# Revit family: IS_Dea_T0598_BIM_GB
name_source: partatom
category: Plumbing Fixtures
revit_build: Autodesk Revit MEP 2012 (Build: 20110309_2315(x64)
units: mm (PartAtom-declared; Revit-internal decimal feet)

## types (2) — shared parameters
Accessories = www.idealspec.co.uk
AreaUnits = millimeters
Assembly Code = C1030200
AssetType = Fixed
BIMObjectName = ISI_IdealStandard_Bidets_Dea-WallHung_T059801
BidetMounting = WallHung
Brand = Ideal Standard
CodePerformance = Vitreous china to BS 3402. Bidet to BS EN 36
Color = White
ConnectionType = Plumbing
Default Elevation = 400 mm  [stored 1.31234 ft]
Description = Dea wall-hung bidet with ceramic waste cover
DrainSize = 32 mm  [stored 0.104987 ft]
DurationUnit = year
ECA = No
ExpectedLife = 30
Features = Wall-hung bidet with ceramic waste cover
Finish = White
IfcExportAs = IfcSanitaryTerminalType
IfcExportType = BIDET
InstallationInstructions = www.idealspec.co.uk/resources.html
LinearUnits = millimeters
ManufacturerURL = www.idealspec.co.uk
Material = Vitreous china
ModelReference = Dea wall-hung bidet with ceramic waste cover
NBSDescription = Bidets
NBSReference = 45-35-70/320
Name = Bidets_Dea-WallHung_IdealStandard
NettWeight = 17.2 Kg
NominalHeight = 310 mm
NominalLength = 540 mm  [stored 1.77165 ft]
NominalWidth = 360 mm
Shape = Sculptured
Size = 310 x 540 x 360 cm
Space = Internal
SpareParts = www.fastpart-spares.co.uk
URL = www.idealspec.co.uk
Uniclass2 = Pr_40_20_06_11
Version = 2
VolumeUnits = Litres
WRAS = No
WarrantyDescription = Manufacturers Warranty
WarrantyDurationParts = 99
WarrantyDurationUnit = year
WaterEfficientProduct = No
zero-valued in all types: CWFU, HWFU, SpilloverLevel, WFU

## per-type parameters (varying)
| type | Model | ModelNumber | NominalDepth | ProductInformation |
| T509801 - Dea Wall Hung Bidet - Gloss White | T509801 | T509801 | 540 mm  [stored 1.77165 ft] | www.idealspec.co.uk/assets/datasheet/T509801 |
| T509883 - Dea Wall Hung Bidet - Matte White | T509883 | T509883 | 0 mm  [stored 0 ft] | www.idealspec.co.uk/assets/datasheet/T509883 |

note: [stored X ft] marks values corroborated as IEEE doubles in the binary element streams (Revit-internal decimal feet)

## geometry (parser evidence)
native form markers: Blend x2, Sweep x2
no freeform markers — native parametric forms only
